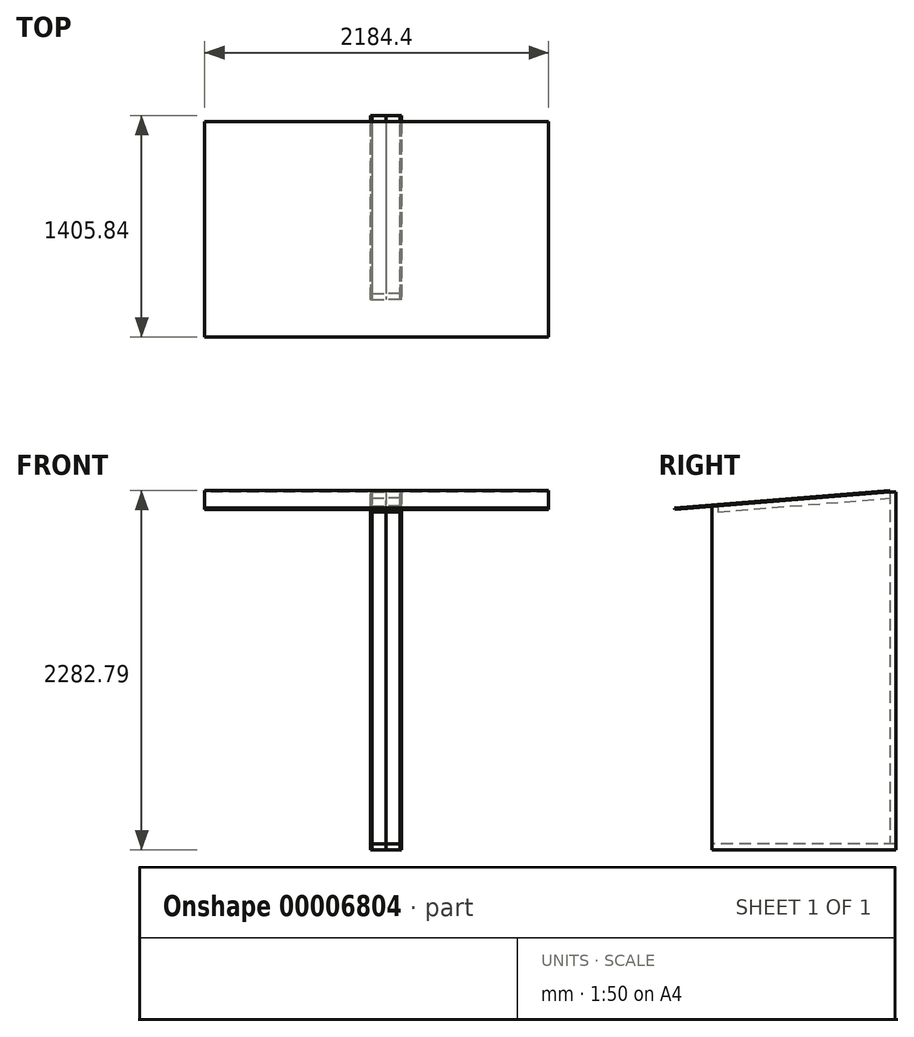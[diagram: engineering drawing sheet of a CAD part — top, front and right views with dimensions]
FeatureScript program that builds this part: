
annotation { "Feature Type Name" : "Feature", "Feature Type Description" : "" }
export const myFeature = defineFeature(function(context is Context, id is Id, definition is map)
    precondition{}
    {
        {
            var Q0;
            Q0=qCreatedBy(makeId("Right.planeOp"),FACE);
            var sketch = newSketch(context, id + "F0", { "sketchPlane" : qUnion([Q0])});
            skLineSegment(sketch, "E0.rect.bottom", {"start": v(-584.2, 1136.65) * mm, "end": v(584.2, 1136.65) * mm, "construction": true});
            skLineSegment(sketch, "E0.rect.top", {"start": v(-584.2, -1136.65) * mm, "end": v(584.2, -1136.65) * mm, "construction": true});
            skLineSegment(sketch, "E0.rect.left", {"start": v(-584.2, 1136.65) * mm, "end": v(-584.2, -1136.65) * mm, "construction": true});
            skLineSegment(sketch, "E0.rect.right", {"start": v(584.2, 1136.65) * mm, "end": v(584.2, -1136.65) * mm, "construction": true});
            skPoint(sketch, "E0.rect.middle", {"position": v(0, 0) * mm});
            skLineSegment(sketch, "E1.bottom", {"start": v(584.2, -1136.65) * mm, "end": v(-584.2, -1136.65) * mm});
            skLineSegment(sketch, "E1.top", {"start": v(584.2, -1098.55) * mm, "end": v(-584.2, -1098.55) * mm});
            skLineSegment(sketch, "E1.left", {"start": v(584.2, -1136.65) * mm, "end": v(584.2, -1098.55) * mm});
            skLineSegment(sketch, "E1.right", {"start": v(-584.2, -1136.65) * mm, "end": v(-584.2, -1098.55) * mm});
            skLineSegment(sketch, "E2.bottom", {"start": v(584.2, 1136.65) * mm, "end": v(546.1, 1136.65) * mm});
            skLineSegment(sketch, "E2.top", {"start": v(584.2, -1098.55) * mm, "end": v(546.1, -1098.55) * mm});
            skLineSegment(sketch, "E2.left", {"start": v(584.2, 1136.65) * mm, "end": v(584.2, -1098.55) * mm});
            skLineSegment(sketch, "E2.right", {"start": v(546.1, 1136.65) * mm, "end": v(546.1, -1098.55) * mm});
            skLineSegment(sketch, "E3.top", {"start": v(-584.2, -1098.55) * mm, "end": v(-546.1, -1098.55) * mm});
            skLineSegment(sketch, "E3.left", {"start": v(-584.2, 1043.43) * mm, "end": v(-584.2, -1098.55) * mm});
            skLineSegment(sketch, "E3.right", {"start": v(-546.1, 1046.57) * mm, "end": v(-546.1, -1098.55) * mm});
            skLineSegment(sketch, "E4", {"start": v(546.1, 1136.65) * mm, "end": v(-546.1, 1046.57) * mm});
            skLineSegment(sketch, "E5", {"start": v(-546.1, 1008.34) * mm, "end": v(546.1, 1098.42) * mm});
            skLineSegment(sketch, "E6", {"start": v(-546.1, 1046.57) * mm, "end": v(-584.2, 1043.43) * mm});
            skLineSegment(sketch, "E7", {"start": v(-473.4, 1052.57) * mm, "end": v(-685.8, 1035.05) * mm, "construction": true});
            skLineSegment(sketch, "E8", {"start": v(-685.8, 1035.05) * mm, "end": v(-685.8, -956.68) * mm, "construction": true});
            skSolve(sketch);
        }
        {
            var Q0;
            {var subQ3=sQuery(id+"F0.wireOp",EDGE,"E3.top");Q0=makeQuery(id+"F0.imprint","IMPRINT",FACE,{"disambiguationData":[TD([[makeQuery(id+"F0.imprint","IMPRINT",EDGE,{"derivedFrom":subQ3}),1.0]])]});}
            var Q1;
            {var subQ3=sQuery(id+"F0.wireOp",EDGE,"E2.bottom");Q1=makeQuery(id+"F0.imprint","IMPRINT",FACE,{"disambiguationData":[TD([[makeQuery(id+"F0.imprint","IMPRINT",EDGE,{"derivedFrom":subQ3}),1.0]])]});}
            extrude(context, id + "F1", {"entities" : qUnion([Q0, Q1]), "depth" : 88.9 * mm});
        }
        {
            var Q0;
            {var subQ1=sQuery(id+"F0.wireOp",EDGE,"E4");Q0=makeQuery(id+"F0.imprint","IMPRINT",FACE,{"disambiguationData":[TD([[makeQuery(id+"F0.imprint","IMPRINT",EDGE,{"derivedFrom":subQ1}),1.0]])]});}
            var Q1;
            Q1=makeQuery(id+"F0.imprint","IMPRINT",FACE,{"disambiguationData":[TD([[makeQuery(id+"F0.imprint","IMPRINT",EDGE,{"derivedFrom":sQuery(id+"F0.wireOp",EDGE,"E1.bottom")}),-1.0]])]});
            extrude(context, id + "F2", {"entities" : qUnion([Q0, Q1]), "depth" : 88.9 * mm});
        }
        {
            var Q0;
            Q0=makeQuery(id+"F1.opExtrude","CAP_FACE",FACE,{"disambiguationData":[OSD([sQuery(id+"F0.wireOp",EDGE,"E2.bottom"),sQuery(id+"F0.wireOp",EDGE,"E2.top"),sQuery(id+"F0.wireOp",EDGE,"E2.left"),sQuery(id+"F0.wireOp",EDGE,"E2.right")])],"isStart":false});
            var sketch = newSketch(context, id + "F3", { "sketchPlane" : qUnion([Q0])});
            skLineSegment(sketch, "E9", {"start": v(546.1, 1136.65) * mm, "end": v(-584.2, 1043.43) * mm});
            skLineSegment(sketch, "E10", {"start": v(-584.2, 1043.43) * mm, "end": v(-584.2, -1136.65) * mm});
            skLineSegment(sketch, "E11", {"start": v(-584.2, -1136.65) * mm, "end": v(584.2, -1136.65) * mm});
            skLineSegment(sketch, "E12", {"start": v(584.2, -1136.65) * mm, "end": v(584.2, 1136.65) * mm});
            skLineSegment(sketch, "E13", {"start": v(584.2, 1136.65) * mm, "end": v(546.1, 1136.65) * mm});
            skSolve(sketch);
        }
        {
            var Q0;
            Q0 = qSketchRegion(id + "F3", true);
            extrude(context, id + "F4", {"entities" : qUnion([Q0]), "depth" : 9.52 * mm});
        }
        {
            var Q0;
            Q0=makeQuery(id+"F1.opExtrude","SWEPT_BODY",BODY,{"disambiguationData":[OSD([sQuery(id+"F0.wireOp",EDGE,"E2.bottom"),sQuery(id+"F0.wireOp",EDGE,"E2.top"),sQuery(id+"F0.wireOp",EDGE,"E2.left"),sQuery(id+"F0.wireOp",EDGE,"E2.right")])]});
            var Q1;
            Q1=makeQuery(id+"F1.opExtrude","SWEPT_BODY",BODY,{"disambiguationData":[OSD([sQuery(id+"F0.wireOp",EDGE,"E3.top"),sQuery(id+"F0.wireOp",EDGE,"E3.left"),sQuery(id+"F0.wireOp",EDGE,"E3.right"),sQuery(id+"F0.wireOp",EDGE,"E6")])]});
            var Q2;
            Q2=makeQuery(id+"F2.opExtrude","SWEPT_BODY",BODY,{"disambiguationData":[OSD([sQuery(id+"F0.wireOp",EDGE,"E1.bottom"),sQuery(id+"F0.wireOp",EDGE,"E1.top"),sQuery(id+"F0.wireOp",EDGE,"E1.left"),sQuery(id+"F0.wireOp",EDGE,"E1.right"),sQuery(id+"F0.wireOp",EDGE,"E2.top"),sQuery(id+"F0.wireOp",EDGE,"E3.top")])]});
            var Q3;
            Q3=makeQuery(id+"F2.opExtrude","SWEPT_BODY",BODY,{"disambiguationData":[OSD([sQuery(id+"F0.wireOp",EDGE,"E2.right"),sQuery(id+"F0.wireOp",EDGE,"E3.right"),sQuery(id+"F0.wireOp",EDGE,"E4"),sQuery(id+"F0.wireOp",EDGE,"E5")])]});
            var Q4;
            Q4=makeQuery(id+"F4.opExtrude","SWEPT_BODY",BODY,{"disambiguationData":[OSD([sQuery(id+"F3.wireOp",EDGE,"E9"),sQuery(id+"F3.wireOp",EDGE,"E10"),sQuery(id+"F3.wireOp",EDGE,"E11"),sQuery(id+"F3.wireOp",EDGE,"E12"),sQuery(id+"F3.wireOp",EDGE,"E13")])]});
            var Q5;
            Q5=qCreatedBy(makeId("Right.planeOp"),FACE);
            mirror(context, id + "F5", {"entities" : qUnion([Q0, Q1, Q2, Q3, Q4]), "mirrorPlane" : qUnion([Q5])});
        }
        {
            var Q0;
            Q0=makeQuery(id+"F2.opExtrude","SWEPT_FACE",FACE,{"disambiguationData":[OSD([sQuery(id+"F0.wireOp",EDGE,"E4")])]});
            var sketch = newSketch(context, id + "F6", { "sketchPlane" : qUnion([Q0])});
            skLineSegment(sketch, "E14.bottom", {"start": v(1031.73, 637.68) * mm, "end": v(-1152.67, 637.68) * mm});
            skLineSegment(sketch, "E14.top", {"start": v(1031.73, -733.92) * mm, "end": v(-1152.67, -733.92) * mm});
            skLineSegment(sketch, "E14.left", {"start": v(1031.73, 637.68) * mm, "end": v(1031.73, -733.92) * mm});
            skLineSegment(sketch, "E14.right", {"start": v(-1152.67, 637.68) * mm, "end": v(-1152.67, -733.92) * mm});
            skSolve(sketch);
        }
        {
            var Q0;
            Q0 = qSketchRegion(id + "F6", true);
            extrude(context, id + "F7", {"entities" : qUnion([Q0]), "depth" : 9.52 * mm});
        }
    });
